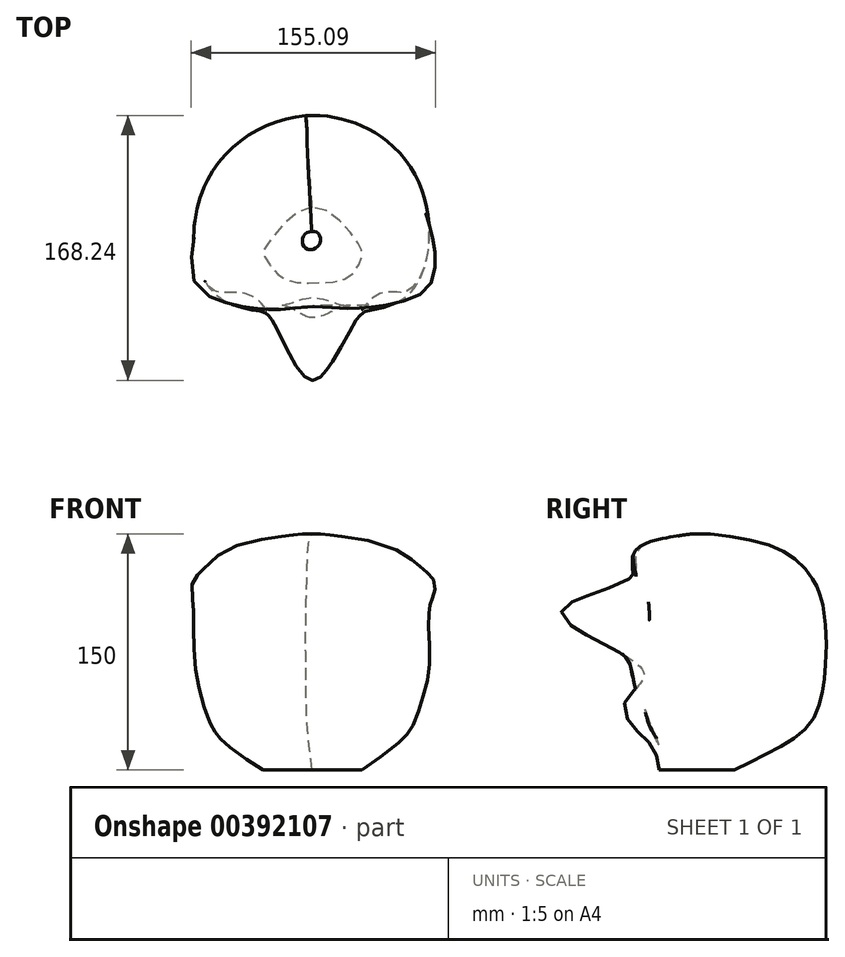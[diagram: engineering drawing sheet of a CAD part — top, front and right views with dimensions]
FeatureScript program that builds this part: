
annotation { "Feature Type Name" : "Feature", "Feature Type Description" : "" }
export const myFeature = defineFeature(function(context is Context, id is Id, definition is map)
    precondition{}
    {
        {
            var Q0;
            Q0=qCreatedBy(makeId("Top.planeOp"),FACE);
            cPlane(context, id + "F0", {"entities" : qUnion([Q0]), "cplaneType" : CPlaneType.OFFSET, "offset" : 15 * mm, "width" : 150 * mm, "height" : 150 * mm});
        }
        {
            var Q0;
            Q0=qCreatedBy(makeId("Top.planeOp"),FACE);
            cPlane(context, id + "F1", {"entities" : qUnion([Q0]), "cplaneType" : CPlaneType.OFFSET, "offset" : 30 * mm, "width" : 150 * mm, "height" : 150 * mm});
        }
        {
            var Q0;
            Q0=qCreatedBy(makeId("Top.planeOp"),FACE);
            cPlane(context, id + "F2", {"entities" : qUnion([Q0]), "cplaneType" : CPlaneType.OFFSET, "offset" : 45 * mm, "width" : 150 * mm, "height" : 150 * mm});
        }
        {
            var Q0;
            Q0=qCreatedBy(makeId("Top.planeOp"),FACE);
            cPlane(context, id + "F3", {"entities" : qUnion([Q0]), "cplaneType" : CPlaneType.OFFSET, "offset" : 60 * mm, "width" : 150 * mm, "height" : 150 * mm});
        }
        {
            var Q0;
            Q0=qCreatedBy(makeId("Top.planeOp"),FACE);
            cPlane(context, id + "F4", {"entities" : qUnion([Q0]), "cplaneType" : CPlaneType.OFFSET, "offset" : 75 * mm, "width" : 150 * mm, "height" : 150 * mm});
        }
        {
            var Q0;
            Q0=qCreatedBy(makeId("Top.planeOp"),FACE);
            cPlane(context, id + "F5", {"entities" : qUnion([Q0]), "cplaneType" : CPlaneType.OFFSET, "offset" : 90 * mm, "width" : 150 * mm, "height" : 150 * mm});
        }
        {
            var Q0;
            Q0=qCreatedBy(makeId("Top.planeOp"),FACE);
            cPlane(context, id + "F6", {"entities" : qUnion([Q0]), "cplaneType" : CPlaneType.OFFSET, "offset" : 105 * mm, "width" : 150 * mm, "height" : 150 * mm});
        }
        {
            var Q0;
            Q0=qCreatedBy(makeId("Top.planeOp"),FACE);
            cPlane(context, id + "F7", {"entities" : qUnion([Q0]), "cplaneType" : CPlaneType.OFFSET, "offset" : 120 * mm, "width" : 150 * mm, "height" : 150 * mm});
        }
        {
            var Q0;
            Q0=qCreatedBy(makeId("Top.planeOp"),FACE);
            cPlane(context, id + "F8", {"entities" : qUnion([Q0]), "cplaneType" : CPlaneType.OFFSET, "offset" : 135 * mm, "width" : 150 * mm, "height" : 150 * mm});
        }
        {
            var Q0;
            Q0=qCreatedBy(makeId("Top.planeOp"),FACE);
            cPlane(context, id + "F9", {"entities" : qUnion([Q0]), "cplaneType" : CPlaneType.OFFSET, "offset" : 150 * mm, "width" : 150 * mm, "height" : 150 * mm});
        }
        {
            var Q0;
            Q0=qCreatedBy(makeId("Top.planeOp"),FACE);
            cPlane(context, id + "F10", {"entities" : qUnion([Q0]), "cplaneType" : CPlaneType.OFFSET, "offset" : 165 * mm, "width" : 150 * mm, "height" : 150 * mm});
        }
        {
            var Q0;
            Q0=qCreatedBy(makeId("Top.planeOp"),FACE);
            cPlane(context, id + "F11", {"entities" : qUnion([Q0]), "cplaneType" : CPlaneType.OFFSET, "offset" : 180 * mm, "width" : 150 * mm, "height" : 150 * mm});
        }
        {
            var Q0;
            Q0=qCreatedBy(id+"F0.planeOp",FACE);
            var sketch = newSketch(context, id + "F12", { "sketchPlane" : qUnion([Q0])});
            skFitSpline(sketch, "E0", {"points": [v(0, 52.37) * mm, v(-28.94, 28.06) * mm, v(-30.97, 23.14) * mm, v(-19.4, 7.8) * mm, v(0, 4.33) * mm, v(23.73, 8.38) * mm, v(31.55, 21.98) * mm, v(28.98, 29.67) * mm, v(0, 52.37) * mm]});
            skSolve(sketch);
        }
        {
            var Q0;
            Q0=qCreatedBy(id+"F1.planeOp",FACE);
            var sketch = newSketch(context, id + "F13", { "sketchPlane" : qUnion([Q0])});
            skFitSpline(sketch, "E1", {"points": [v(0, 81.83) * mm, v(-46.5, 45.87) * mm, v(-49.5, 8.38) * mm, v(-27.5, 4.33) * mm, v(0, 0) * mm, v(28.07, 4.33) * mm, v(47.75, 10.7) * mm, v(47.16, 47.05) * mm, v(0, 81.83) * mm]});
            skSolve(sketch);
        }
        {
            var Q0;
            Q0=qCreatedBy(id+"F2.planeOp",FACE);
            var sketch = newSketch(context, id + "F14", { "sketchPlane" : qUnion([Q0])});
            skFitSpline(sketch, "E2", {"points": [v(0, 100.8) * mm, v(-57.96, 58.12) * mm, v(-56.48, 0) * mm, v(-23.9, -2.17) * mm, v(0, -14.12) * mm, v(26.88, -2.17) * mm, v(55.94, 0) * mm, v(58.62, 58.12) * mm, v(0, 100.8) * mm]});
            skSolve(sketch);
        }
        {
            var Q0;
            Q0=qCreatedBy(id+"F3.planeOp",FACE);
            var sketch = newSketch(context, id + "F15", { "sketchPlane" : qUnion([Q0])});
            skFitSpline(sketch, "E3", {"points": [v(0, 107.12) * mm, v(-61.52, 63.65) * mm, v(-61.37, 0) * mm, v(-23.9, -8.15) * mm, v(0, -16.3) * mm, v(26.88, -9.23) * mm, v(60.56, 0) * mm, v(62.57, 63.65) * mm, v(0, 107.12) * mm]});
            skSolve(sketch);
        }
        {
            var Q0;
            Q0=qCreatedBy(id+"F4.planeOp",FACE);
            var sketch = newSketch(context, id + "F16", { "sketchPlane" : qUnion([Q0])});
            skFitSpline(sketch, "E4", {"points": [v(0, 109.5) * mm, v(-65.47, 65.23) * mm, v(-64.28, 0) * mm, v(-24.77, -11.83) * mm, v(0, -5.11) * mm, v(27, -11.83) * mm, v(63.76, 0) * mm, v(66.13, 66.81) * mm, v(0, 109.5) * mm]});
            skSolve(sketch);
        }
        {
            var Q0;
            Q0=qCreatedBy(id+"F7.planeOp",FACE);
            var sketch = newSketch(context, id + "F17", { "sketchPlane" : qUnion([Q0])});
            skFitSpline(sketch, "E5", {"points": [v(0, 108.4) * mm, v(-65.83, 64.87) * mm, v(-68.3, 0) * mm, v(-35.44, -6.58) * mm, v(0, -54.22) * mm, v(39.3, -5.35) * mm, v(67.22, 0) * mm, v(66, 66.1) * mm, v(0, 108.4) * mm]});
            skSolve(sketch);
        }
        {
            var Q0;
            Q0=qCreatedBy(id+"F8.planeOp",FACE);
            var sketch = newSketch(context, id + "F18", { "sketchPlane" : qUnion([Q0])});
            skFitSpline(sketch, "E6", {"points": [v(0, 102.65) * mm, v(-61.72, 62.82) * mm, v(-69.94, 0) * mm, v(-24.76, -12.33) * mm, v(0, -16.85) * mm, v(26.16, -10.7) * mm, v(71.33, 0) * mm, v(63.94, 63.23) * mm, v(0, 102.65) * mm]});
            skSolve(sketch);
        }
        {
            var Q0;
            Q0=qCreatedBy(id+"F9.planeOp",FACE);
            var sketch = newSketch(context, id + "F19", { "sketchPlane" : qUnion([Q0])});
            skFitSpline(sketch, "E7", {"points": [v(0, 89.51) * mm, v(-59.26, 59.94) * mm, v(-44.48, 0) * mm, v(-24.76, -12.33) * mm, v(0, -10.7) * mm, v(26.16, -11.92) * mm, v(45.46, 0) * mm, v(59.01, 59.94) * mm, v(0, 89.51) * mm]});
            skSolve(sketch);
        }
        {
            var Q0;
            Q0=qCreatedBy(id+"F10.planeOp",FACE);
            var sketch = newSketch(context, id + "F20", { "sketchPlane" : qUnion([Q0])});
            skFitSpline(sketch, "E8", {"points": [v(0, 36.92) * mm, v(-4.28, 35.59) * mm, v(-6.23, 31.17) * mm, v(-4.8, 26.76) * mm, v(0, 25.42) * mm, v(4.04, 27.89) * mm, v(5.17, 31.27) * mm, v(3.83, 35.8) * mm, v(0, 36.92) * mm]});
            skSolve(sketch);
        }
        {
            var Q0;
            Q0 = qSketchRegion(id + "F12", true);
            var Q1;
            Q1 = qSketchRegion(id + "F13", true);
            var Q2;
            Q2 = qSketchRegion(id + "F14", true);
            var Q3;
            Q3 = qSketchRegion(id + "F15", true);
            var Q4;
            Q4 = qSketchRegion(id + "F16", true);
            var Q5;
            Q5 = qSketchRegion(id + "F17", true);
            var Q6;
            Q6 = qSketchRegion(id + "F18", true);
            var Q7;
            Q7 = qSketchRegion(id + "F19", true);
            var Q8;
            Q8 = qSketchRegion(id + "F20", true);
            loft(context, id + "F21", {"sheetProfilesArray" : [{ "sheetProfileEntities" : qUnion([Q0]) }, { "sheetProfileEntities" : qUnion([Q1]) }, { "sheetProfileEntities" : qUnion([Q2]) }, { "sheetProfileEntities" : qUnion([Q3]) }, { "sheetProfileEntities" : qUnion([Q4]) }, { "sheetProfileEntities" : qUnion([Q5]) }, { "sheetProfileEntities" : qUnion([Q6]) }, { "sheetProfileEntities" : qUnion([Q7]) }, { "sheetProfileEntities" : qUnion([Q8]) }]});
        }
    });
